# Revit family: H-202_RFA
name_source: partatom
category: Aparatos sanitarios
units: mm (PartAtom-declared; Revit-internal decimal feet)

## family parameters
Compartido = No
Corte con vacíos al cargar = No
Cota de conector redondo = Diámetro de uso
Número OmniClass = 23.45.00.00
Punto de cálculo de habitación = No
Se basa en plano de trabajo = No
Siempre vertical = Sí
Tipo de pieza = Normal
Título OmniClass = Sanitary, Laundry, and Cleaning Equipment

## types (2) — shared parameters
Brass Chromed = Brass
Comentarios de tipo = Showerheads
Data Sheet = https://helvex.com.mx
Elevación por defecto = 75"
Fabricante = HELVEX
Inlet Threads = ½" - 14 NPT
Instructive = https://helvex.com.mx
Max. Working Pressure = 85.3 psi
Total Length = 7"
URL = https://helvex.com.mx

## per-type parameters (varying)
| type | Descripción | Features | Flow Rate | Imagen de tipo | Min. Working Pressure | Total Width |
| H-201 | Regadera de Baja, Media y Alta Presión Economizador Dinámico de Agua Cumple con la Norma NOM-008-CONAGUA-1998 Con Sistema Anticalcáreo Incluye Nudo Móvil | Regadera de Baja, Media y Alta Presión Economizador Dinámico de Agua Cumple con la Norma NOM-008-CONAGUA-1998 Con Sistema Anticalcáreo Incluye Nudo Móvil | 0.0 gal/min | <Ninguno> | 2.8 psi | 4" |
| H-202 | Regadera con chorro vigorizante Iguazú | Regadera de chorro vigorizante. Acabado cromo. Presión mínima requerida 1.50 kg/cm². Incluye brazo y chapetón. Consumo máximo de agua 9.5 L/min. | 2.5 gal/min | H-202.PNG | 21.3 psi | 9" |

note: column(s) folded — value = type name in every type: Modelo

## geometry (parser evidence)
native form markers: Sweep x3
no freeform markers — native parametric forms only
